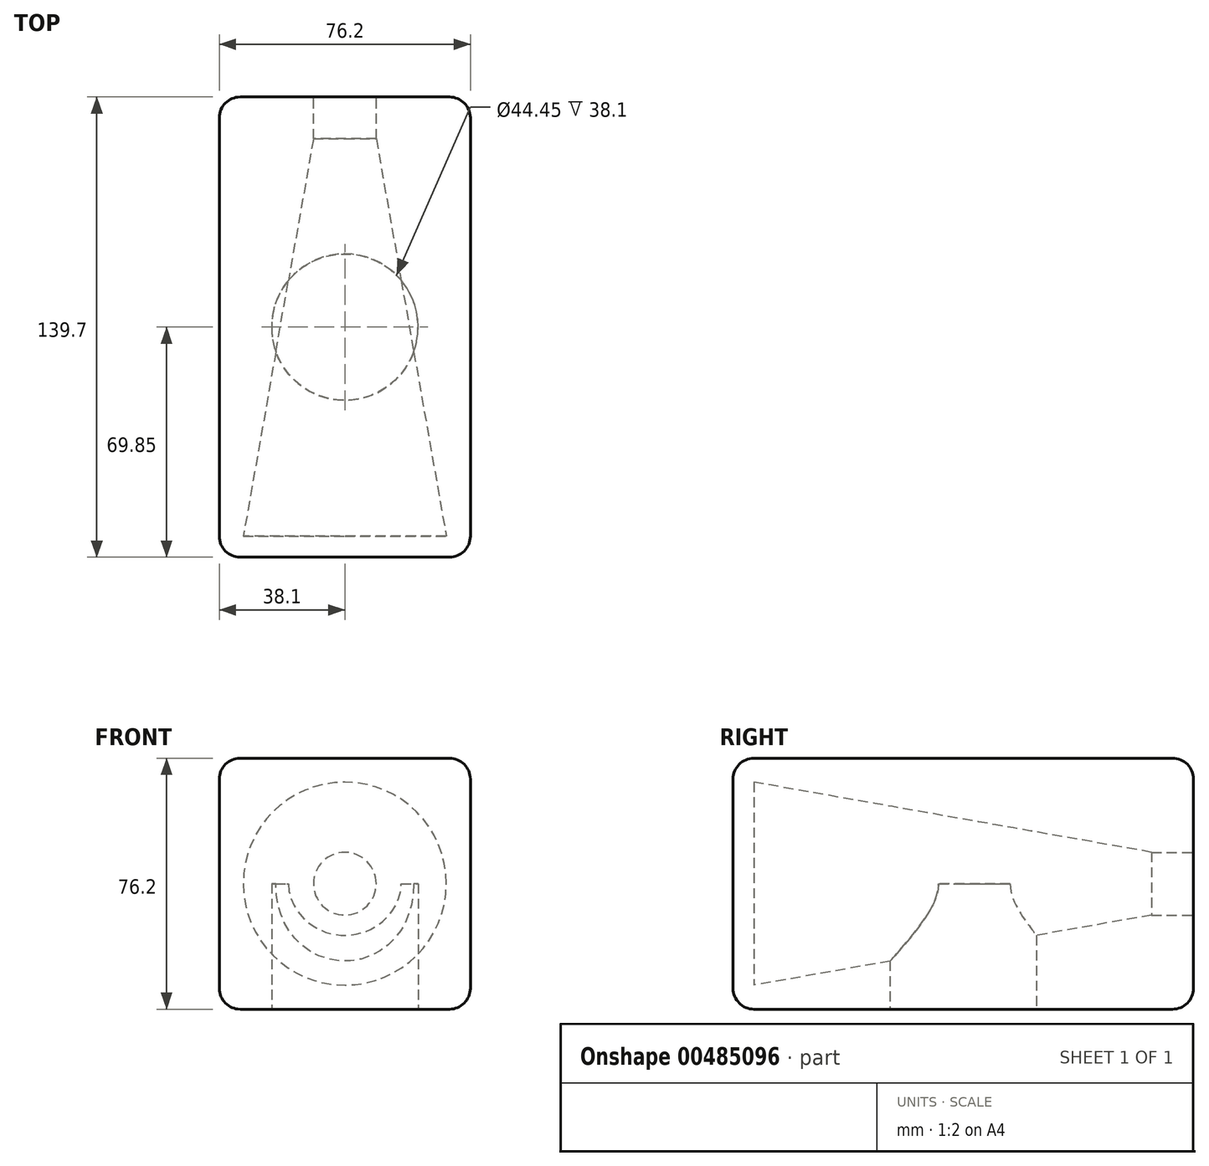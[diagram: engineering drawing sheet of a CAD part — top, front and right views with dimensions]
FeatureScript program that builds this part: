
annotation { "Feature Type Name" : "Feature", "Feature Type Description" : "" }
export const myFeature = defineFeature(function(context is Context, id is Id, definition is map)
    precondition{}
    {
        {
            var Q0;
            Q0=qCreatedBy(makeId("Top.planeOp"),FACE);
            var sketch = newSketch(context, id + "F0", { "sketchPlane" : qUnion([Q0])});
            skLineSegment(sketch, "E0.bottom", {"start": v(38.1, 69.85) * mm, "end": v(-38.1, 69.85) * mm});
            skLineSegment(sketch, "E0.top", {"start": v(38.1, -69.85) * mm, "end": v(-38.1, -69.85) * mm});
            skLineSegment(sketch, "E0.left", {"start": v(38.1, 69.85) * mm, "end": v(38.1, -69.85) * mm});
            skLineSegment(sketch, "E0.right", {"start": v(-38.1, 69.85) * mm, "end": v(-38.1, -69.85) * mm});
            skPoint(sketch, "E0.middle", {"position": v(0, 0) * mm});
            skSolve(sketch);
        }
        {
            var Q0;
            Q0=makeQuery(id+"F0.imprint","IMPRINT",FACE,{"disambiguationData":[TD([[makeQuery(id+"F0.imprint","IMPRINT",EDGE,{"derivedFrom":sQuery(id+"F0.wireOp",EDGE,"E0.bottom")}),1.0]])]});
            extrude(context, id + "F1", {"entities" : qUnion([Q0]), "depth" : 76.2 * mm});
        }
        {
            var Q0;
            Q0=makeQuery(id+"F1.opExtrude","CAP_FACE",FACE,{"disambiguationData":[OSD([sQuery(id+"F0.wireOp",EDGE,"E0.bottom"),sQuery(id+"F0.wireOp",EDGE,"E0.top"),sQuery(id+"F0.wireOp",EDGE,"E0.left"),sQuery(id+"F0.wireOp",EDGE,"E0.right")])],"isStart":true});
            var sketch = newSketch(context, id + "F2", { "sketchPlane" : qUnion([Q0])});
            skCircle(sketch, "E1", {"center": v(0, 0) * mm, "radius": 22.23 * mm});
            skSolve(sketch);
        }
        {
            var Q0;
            Q0=makeQuery(id+"F1.opExtrude","CAP_EDGE",EDGE,{"disambiguationData":[OSD([sQuery(id+"F0.wireOp",EDGE,"E0.left")])],"isStart":false});
            var Q1;
            Q1=makeQuery(id+"F1.opExtrude","CAP_EDGE",EDGE,{"disambiguationData":[OSD([sQuery(id+"F0.wireOp",EDGE,"E0.bottom")])],"isStart":false});
            var Q2;
            Q2=makeQuery(id+"F1.opExtrude","CAP_EDGE",EDGE,{"disambiguationData":[OSD([sQuery(id+"F0.wireOp",EDGE,"E0.right")])],"isStart":false});
            var Q3;
            Q3=makeQuery(id+"F1.opExtrude","CAP_EDGE",EDGE,{"disambiguationData":[OSD([sQuery(id+"F0.wireOp",EDGE,"E0.top")])],"isStart":false});
            var Q4;
            Q4=makeQuery(id+"F1.opExtrude","SWEPT_EDGE",EDGE,{"disambiguationData":[OSD([sQuery(id+"F0.wireOp",EDGE,"E0.bottom"),sQuery(id+"F0.wireOp",EDGE,"E0.left")])]});
            var Q5;
            Q5=makeQuery(id+"F1.opExtrude","SWEPT_EDGE",EDGE,{"disambiguationData":[OSD([sQuery(id+"F0.wireOp",EDGE,"E0.bottom"),sQuery(id+"F0.wireOp",EDGE,"E0.right")])]});
            var Q6;
            Q6=makeQuery(id+"F1.opExtrude","CAP_EDGE",EDGE,{"disambiguationData":[OSD([sQuery(id+"F0.wireOp",EDGE,"E0.bottom")])],"isStart":true});
            var Q7;
            Q7=makeQuery(id+"F1.opExtrude","SWEPT_FACE",FACE,{"disambiguationData":[OSD([sQuery(id+"F0.wireOp",EDGE,"E0.left")])]});
            var Q8;
            Q8=makeQuery(id+"F1.opExtrude","CAP_EDGE",EDGE,{"disambiguationData":[OSD([sQuery(id+"F0.wireOp",EDGE,"E0.top")])],"isStart":true});
            var Q9;
            Q9=makeQuery(id+"F1.opExtrude","SWEPT_EDGE",EDGE,{"disambiguationData":[OSD([sQuery(id+"F0.wireOp",EDGE,"E0.top"),sQuery(id+"F0.wireOp",EDGE,"E0.right")])]});
            var Q10;
            Q10=makeQuery(id+"F1.opExtrude","CAP_EDGE",EDGE,{"disambiguationData":[OSD([sQuery(id+"F0.wireOp",EDGE,"E0.right")])],"isStart":true});
            fillet(context, id + "F3", {"entities" : qUnion([Q0, Q1, Q2, Q3, Q4, Q5, Q6, Q7, Q8, Q9, Q10]), "radius" : 6.35 * mm, "tangentPropagation" : true, "allowEdgeOverflow" : false});
        }
        {
            var Q0;
            Q0 = qSketchRegion(id + "F2", true);
            extrude(context, id + "F4", {"entities" : qUnion([Q0]), "operationType" : NewBodyOperationType.REMOVE, "oppositeDirection" : true, "depth" : 12.7 * mm});
        }
        {
            var Q0;
            Q0=makeQuery(id+"F4.boolean.opBoolean","COPY",FACE,{"derivedFrom":makeQuery(id+"F4.opExtrude","CAP_FACE",FACE,{"disambiguationData":[OSD([sQuery(id+"F2.wireOp",EDGE,"E1")])],"isStart":false})});
            var sketch = newSketch(context, id + "F5", { "sketchPlane" : qUnion([Q0])});
            skCircle(sketch, "E2", {"center": v(0, 0) * mm, "radius": 22.23 * mm});
            skSolve(sketch);
        }
        {
            var Q0;
            Q0=makeQuery(id+"F1.opExtrude","SWEPT_FACE",FACE,{"disambiguationData":[OSD([sQuery(id+"F0.wireOp",EDGE,"E0.bottom")])]});
            var sketch = newSketch(context, id + "F6", { "sketchPlane" : qUnion([Q0])});
            skCircle(sketch, "E3", {"center": v(0, 38.1) * mm, "radius": 9.53 * mm});
            skSolve(sketch);
        }
        {
            var Q0;
            Q0 = qSketchRegion(id + "F6", true);
            extrude(context, id + "F7", {"entities" : qUnion([Q0]), "operationType" : NewBodyOperationType.REMOVE, "oppositeDirection" : true, "depth" : 12.7 * mm});
        }
        {
            var Q0;
            Q0=makeQuery(id+"F7.boolean.opBoolean","COPY",FACE,{"derivedFrom":makeQuery(id+"F7.opExtrude","CAP_FACE",FACE,{"disambiguationData":[OSD([sQuery(id+"F6.wireOp",EDGE,"E3")])],"isStart":false})});
            var sketch = newSketch(context, id + "F8", { "sketchPlane" : qUnion([Q0])});
            skCircle(sketch, "E4", {"center": v(0, 38.1) * mm, "radius": 9.53 * mm});
            skSolve(sketch);
        }
        {
            var Q0;
            Q0 = qSketchRegion(id + "F8", true);
            extrude(context, id + "F9", {"entities" : qUnion([Q0]), "operationType" : NewBodyOperationType.REMOVE, "oppositeDirection" : true, "depth" : 120.65 * mm, "hasDraft" : true, "draftAngle" : 10 * degree});
        }
        {
            var Q0;
            Q0=makeQuery(id+"F5.imprint","IMPRINT",FACE,{"disambiguationData":[TD([[makeQuery(id+"F5.imprint","IMPRINT",EDGE,{"derivedFrom":sQuery(id+"F5.wireOp",EDGE,"E2")}),1.0]])]});
            var Q1;
            Q1 = qSketchRegion(id + "F5", true);
            extrude(context, id + "F10", {"entities" : qUnion([Q0, Q1]), "operationType" : NewBodyOperationType.REMOVE, "oppositeDirection" : true, "depth" : 25.4 * mm});
        }
    });
